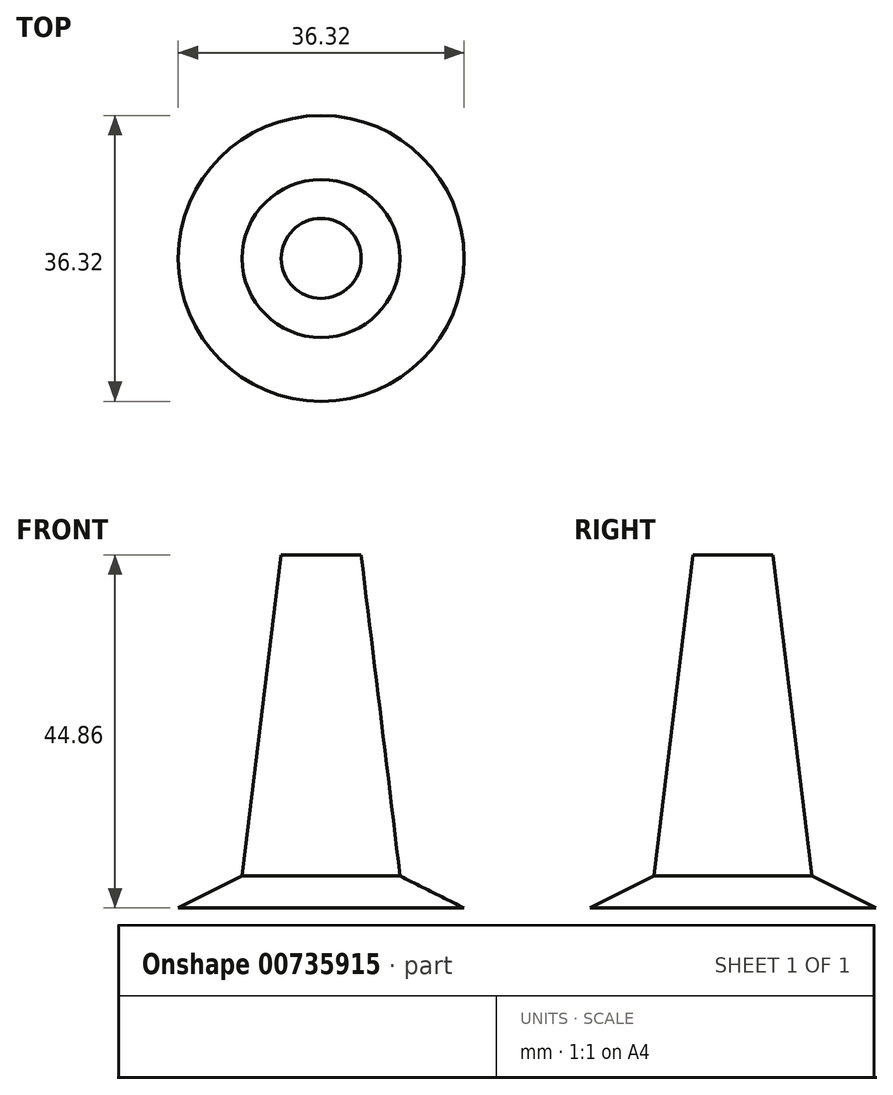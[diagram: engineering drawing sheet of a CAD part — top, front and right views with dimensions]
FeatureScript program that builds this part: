
annotation { "Feature Type Name" : "Feature", "Feature Type Description" : "" }
export const myFeature = defineFeature(function(context is Context, id is Id, definition is map)
    precondition{}
    {
        {
            var Q0;
            Q0=qCreatedBy(makeId("Front.planeOp"),FACE);
            var sketch = newSketch(context, id + "F0", { "sketchPlane" : qUnion([Q0])});
            skLineSegment(sketch, "E0", {"start": v(0, 26.15) * mm, "end": v(5.08, 26.15) * mm});
            skLineSegment(sketch, "E1", {"start": v(5.08, 26.15) * mm, "end": v(10.03, -14.65) * mm});
            skLineSegment(sketch, "E2", {"start": v(0, 26.15) * mm, "end": v(0, -13.55) * mm});
            skLineSegment(sketch, "E3", {"start": v(0, -13.55) * mm, "end": v(10.03, -14.65) * mm});
            skLineSegment(sketch, "E4", {"start": v(10.03, -14.65) * mm, "end": v(18.16, -18.71) * mm});
            skLineSegment(sketch, "E5", {"start": v(18.16, -18.71) * mm, "end": v(0, -18.71) * mm});
            skLineSegment(sketch, "E6", {"start": v(0, -13.55) * mm, "end": v(0, -18.71) * mm});
            skSolve(sketch);
        }
        {
            var Q0;
            Q0 = qSketchRegion(id + "F0", true);
            var Q1;
            Q1=sQuery(id+"F0.wireOp",EDGE,"E2");
            revolve(context, id + "F1", {"surfaceOperationType" : NewSurfaceOperationType.NEW, "entities" : qUnion([Q0]), "axis" : qUnion([Q1]), "revolveType" : RevolveType.FULL});
        }
    });
